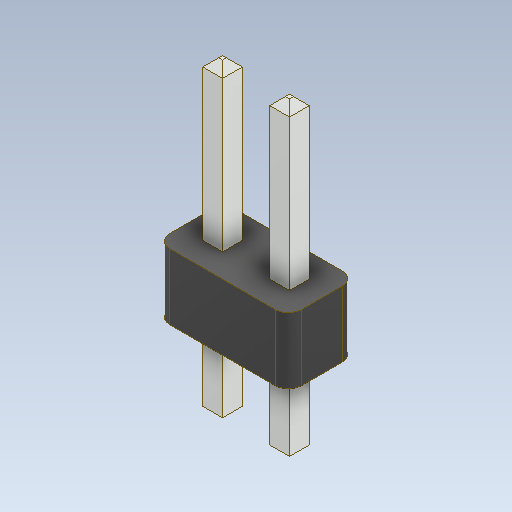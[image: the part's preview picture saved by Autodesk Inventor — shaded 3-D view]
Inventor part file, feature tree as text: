
AUTODESK INVENTOR PART (.ipt)
format: ipt  version: 2020 (Build 240168000, 168)  size: 119,808 bytes
history: native  units: in
note: dims shown in document units (in); Inventor stores cm internally (conversion verified against a paired STEP export)
features: chamfer x1
ambient origin geometry x8: Origin, YZ Plane, XZ Plane, XY Plane, X Axis, Y Axis, Z Axis, Center Point
bodies: Solid1 (feature_tree)
feature tree (1):
  chamfer  "Chamfer1"  [1 undecoded]
note: 1 required parameter value undecoded (feature->parameter linkage not recoverable at this tier; creation-order binding heuristic only, values carry confidence <= 0.55)
